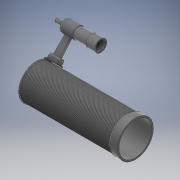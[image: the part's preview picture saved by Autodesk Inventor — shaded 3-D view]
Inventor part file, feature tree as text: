
AUTODESK INVENTOR PART (.ipt)
format: ipt  version: 2022 (Build 260153000, 153)  size: 421,376 bytes
history: native  units: mm
features: sketch x25, extrude x23, fillet x8, chamfer x5, plane x2, hole x1
ambient origin geometry x8: Origin, YZ Plane, XZ Plane, XY Plane, X Axis, Y Axis, Z Axis, Center Point
bodies: Body1 (feature_tree), Body2 (feature_tree)
feature tree (64):
  extrude  "Extrusion2"  Depth=400.0mm TaperAngle=0.0deg
  extrude  "Extrusion3"  Depth=40.0mm TaperAngle=0.0deg
  plane  "Work Plane1"
  extrude  "Extrusion4"  Depth=20.0mm TaperAngle=0.0deg
  chamfer  "Chamfer1"  Distance=40.0mm
  sketch  "Sketch7"  dims[d16=0.8mm d17=8.0mm d18=2.0mm d19=60.0deg]
  extrude  "Extrusion5"  Depth=8.0mm TaperAngle=60.0deg
  extrude  "Extrusion6"  TaperAngle=0.0deg  [1 undecoded]
  fillet  "Fillet1"  Radius=200.0mm
  chamfer  "Chamfer2"  Distance=6.0mm
  fillet  "Fillet2"  Radius=10.0mm
  extrude  "Extrusion7"  Depth=0.5mm
  sketch  "Sketch8"  dims[d20=1.0mm d21=0.0mm d22=0.0mm d23=200.0mm]
  extrude  "Extrusion8"  Depth=0.5mm
  extrude  "Extrusion9"  Depth=73.0mm TaperAngle=0.0deg
  extrude  "Extrusion10"  Depth=8.0mm TaperAngle=30.0deg
  fillet  "Fillet3"  [1 undecoded]
  fillet  "Fillet4"  Radius=10.0mm
  fillet  "Fillet5"  Radius=40.0mm
  extrude  "Extrusion11"  Depth=2.0mm TaperAngle=0.0deg
  extrude  "Extrusion12"  Depth=16.0mm
  chamfer  "Chamfer3"  Distance=32.0mm
  chamfer  "Chamfer4"  Distance=100.0mm
  chamfer  "Chamfer5"  Distance=40.0mm
  plane  "Work Plane3"
  extrude  "Extrusion13"  Depth=1.0mm
  extrude  "Extrusion14"  TaperAngle=45.0deg  [1 undecoded]
  extrude  "Extrusion15"  Depth=400.0mm TaperAngle=0.0deg
  extrude  "Extrusion16"  Depth=10.0mm TaperAngle=0.0deg
  extrude  "Extrusion17"  TaperAngle=0.0deg  [1 undecoded]
  extrude  "Extrusion18"  Depth=0.5mm
  extrude  "Extrusion19"  [1 undecoded]
  extrude  "Extrusion20"  [1 undecoded]
  fillet  "Fillet6"  [1 undecoded]
  fillet  "Fillet7"  [1 undecoded]
  fillet  "Fillet8"  [1 undecoded]
  extrude  "Extrusion27"  [1 undecoded]
  sketch  "Sketch31"
  extrude  "Extrusion28"  [1 undecoded]
  extrude  "Extrusion29"  [1 undecoded]
  sketch  "Sketch34"
  hole  "Hole1"  [1 undecoded]
  extrude  "Extrusion30"  [1 undecoded]
  sketch  "Sketch3"  dims[d2=4.0mm d3=0.0mm d4=400.0mm d5=0.0mm]
  sketch  "Sketch4"  dims[d6=400.0mm d7=40.0mm d8=0.0mm]
  sketch  "Sketch5"  dims[d9=4.0mm d10=2.0mm d11=60.0deg d12=20.0mm d13=0.0mm d14=40.0mm d15=0.0mm]
  sketch  "Sketch9"  dims[d24=135.0deg d25=6.0mm d26=0.0mm d27=10.0mm d28=0.0mm]
  sketch  "Sketch10"  dims[d29=50.0mm d30=0.0mm d31=0.5mm]
  sketch  "Sketch11"  dims[d32=2.0mm d33=0.5mm]
  sketch  "Sketch12"  dims[d34=20.0mm d35=0.0mm d36=73.0mm d37=0.0mm]
  sketch  "Sketch13"  dims[d38=70.0mm d39=2.0mm d40=0.698132mm d41=8.0mm d42=2.0mm d43=30.0deg]
  sketch  "Sketch15"  dims[d44=8.0mm d45=2.0mm d46=30.0deg d47=0.0mm d48=10.0mm d49=0.0mm d50=40.0mm d51=0.0mm]
  sketch  "Sketch16"  dims[d52=18.0mm d53=0.0mm d54=2.0mm d55=0.0mm]
  sketch  "Sketch17"  dims[d56=6.0mm d57=0.0mm d58=16.0mm d59=32.0mm d60=0.0mm d61=100.0mm d62=0.0mm d63=40.0mm d64=0.0mm]
  sketch  "Sketch18"  dims[d65=0.5mm d66=1.0mm]
  sketch  "Sketch19"  dims[d67=0.5mm d86=45.0deg]
  sketch  "Sketch20"  dims[d87=45.0deg d88=400.0mm d89=0.0mm]
  sketch  "Sketch21"  dims[d90=10.0mm d91=0.0mm d92=10.0mm d93=0.0mm]
  sketch  "Sketch22"  dims[d94=4.917mm d95=26.0mm d96=4.0mm d97=2.0mm d98=90.0deg d99=8.0mm d100=0.0mm d101=0.0mm d102=0.0mm]
  sketch  "Sketch30"  dims[d0=0.5mm d1=0.872665mm]
  sketch  "Sketch32"
  sketch  "Sketch33"
  sketch  "Sketch35"
  sketch  "Sketch36"
note: 14 required parameter values undecoded (feature->parameter linkage not recoverable at this tier; creation-order binding heuristic only, values carry confidence <= 0.55)
